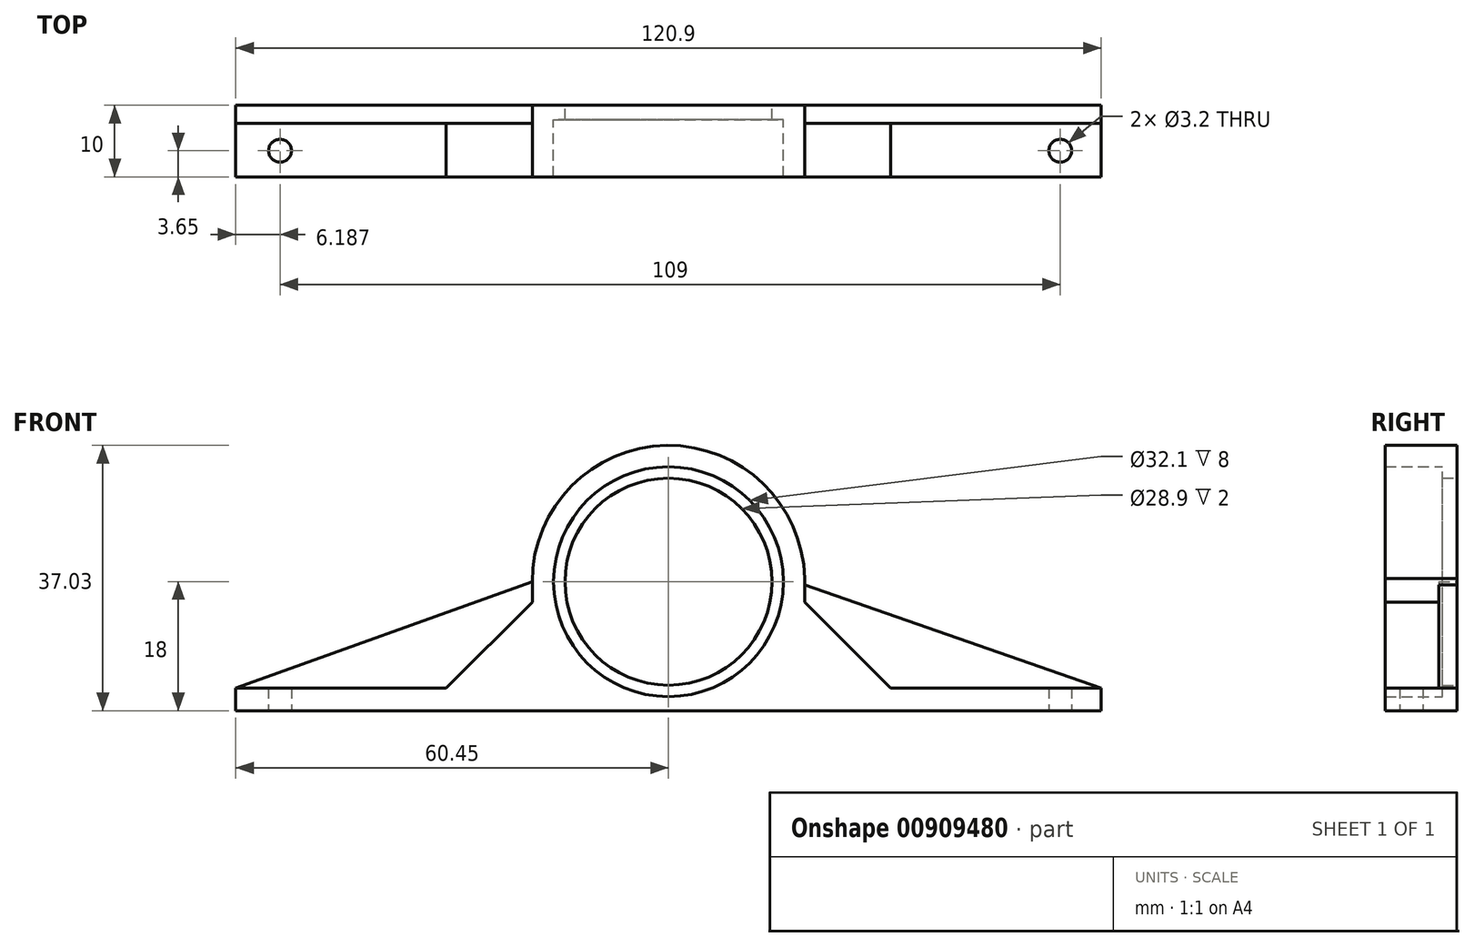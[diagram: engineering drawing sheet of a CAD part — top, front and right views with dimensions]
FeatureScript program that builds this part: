
annotation { "Feature Type Name" : "Feature", "Feature Type Description" : "" }
export const myFeature = defineFeature(function(context is Context, id is Id, definition is map)
    precondition{}
    {
        {
            var Q0;
            Q0=qCreatedBy(makeId("Front.planeOp"),FACE);
            var sketch = newSketch(context, id + "F0", { "sketchPlane" : qUnion([Q0])});
            skLineSegment(sketch, "E0.bottom", {"start": v(-60.45, 0) * mm, "end": v(-15.87, 0) * mm});
            skLineSegment(sketch, "E0.top", {"start": v(-60.45, 3.18) * mm, "end": v(-19.03, 3.18) * mm});
            skLineSegment(sketch, "E0.left", {"start": v(-60.45, 0) * mm, "end": v(-60.45, 3.18) * mm});
            skLineSegment(sketch, "E0.right", {"start": v(60.45, 0) * mm, "end": v(60.45, 3.18) * mm});
            skLineSegment(sketch, "E1.trimOffspring", {"start": v(19.02, 3.18) * mm, "end": v(60.45, 3.18) * mm});
            skLineSegment(sketch, "E2.trimOffspring", {"start": v(15.85, 0) * mm, "end": v(60.45, 0) * mm});
            skArc(sketch, "E3", {"start": v(15.85, 20.53) * mm, "mid": v(-1.27, 34) * mm, "end": v(-16.05, 18) * mm});
            skArc(sketch, "E4", {"start": v(19.02, 18.46) * mm, "mid": v(-0.23, 37.03) * mm, "end": v(-19.03, 18) * mm});
            skLineSegment(sketch, "E5", {"start": v(-19.03, 18) * mm, "end": v(-19.03, 3.18) * mm});
            skLineSegment(sketch, "E6", {"start": v(15.85, 20.53) * mm, "end": v(15.85, 20.53) * mm});
            skLineSegment(sketch, "E7", {"start": v(19.02, 18.46) * mm, "end": v(19.02, 3.18) * mm});
            skPoint(sketch, "E8.orphan", {"position": v(-19.03, 0) * mm});
            skPoint(sketch, "E9.orphan", {"position": v(19.02, 0) * mm});
            skLineSegment(sketch, "E10", {"start": v(0, 18) * mm, "end": v(0, 18) * mm});
            skCircle(sketch, "E11", {"center": v(0, 18) * mm, "radius": 16.05 * mm});
            skArc(sketch, "E12", {"start": v(19.02, 17.54) * mm, "mid": v(0.23, 37.03) * mm, "end": v(-19.03, 18) * mm});
            skLineSegment(sketch, "E13", {"start": v(-15.87, 0) * mm, "end": v(15.85, 0) * mm});
            skCircle(sketch, "E14", {"center": v(0, 18) * mm, "radius": 14.45 * mm});
            skLineSegment(sketch, "E15", {"start": v(-19.03, 18) * mm, "end": v(-60.45, 3.18) * mm});
            skLineSegment(sketch, "E16", {"start": v(19.02, 17.54) * mm, "end": v(60.45, 3.18) * mm});
            skLineSegment(sketch, "E17", {"start": v(19.02, 15.18) * mm, "end": v(31.03, 3.18) * mm});
            skLineSegment(sketch, "E18", {"start": v(-19.03, 15.18) * mm, "end": v(-31.03, 3.18) * mm});
            skSolve(sketch);
        }
        {
            var Q0;
            Q0=makeQuery(id+"F0.imprint","IMPRINT",FACE,{"disambiguationData":[TD([[makeQuery(id+"F0.imprint","IMPRINT",EDGE,{"derivedFrom":sQuery(id+"F0.wireOp",EDGE,"E0.top")}),-1.0]])]});
            extrude(context, id + "F1", {"entities" : qUnion([Q0]), "depth" : 10 * mm, "offsetDistance" : 25.4 * mm});
        }
        {
            var Q0;
            Q0=makeQuery(id+"F0.imprint","IMPRINT",FACE,{"disambiguationData":[TD([[makeQuery(id+"F0.imprint","IMPRINT",EDGE,{"derivedFrom":sQuery(id+"F0.wireOp",EDGE,"E3")}),1.0]])]});
            extrude(context, id + "F2", {"entities" : qUnion([Q0]), "operationType" : NewBodyOperationType.ADD, "depth" : 1.59 * mm, "offsetDistance" : 25.4 * mm});
        }
        {
            var Q0;
            Q0=makeQuery(id+"F1.opExtrude","SWEPT_FACE",FACE,{"disambiguationData":[OSD([sQuery(id+"F0.wireOp",EDGE,"E0.bottom")])]});
            var sketch = newSketch(context, id + "F3", { "sketchPlane" : qUnion([Q0])});
            skCircle(sketch, "E19", {"center": v(54.74, 6.35) * mm, "radius": 1.6 * mm});
            skCircle(sketch, "E20", {"center": v(-54.26, 6.35) * mm, "radius": 1.6 * mm});
            skSolve(sketch);
        }
        {
            var Q0;
            Q0=makeQuery(id+"F3.imprint","IMPRINT",FACE,{"disambiguationData":[TD([[makeQuery(id+"F3.imprint","IMPRINT",EDGE,{"derivedFrom":sQuery(id+"F3.wireOp",EDGE,"E20")}),1.0]])]});
            var Q1;
            Q1=makeQuery(id+"F3.imprint","IMPRINT",FACE,{"disambiguationData":[TD([[makeQuery(id+"F3.imprint","IMPRINT",EDGE,{"derivedFrom":sQuery(id+"F3.wireOp",EDGE,"E19")}),1.0]])]});
            var Q2;
            Q2=sQuery(id+"F3.wireOp",EDGE,"E20");
            var Q3;
            Q3=sQuery(id+"F3.wireOp",EDGE,"E19");
            extrude(context, id + "F4", {"entities" : qUnion([Q0, Q1]), "operationType" : NewBodyOperationType.REMOVE, "surfaceEntities" : qUnion([Q2, Q3]), "oppositeDirection" : true, "depth" : 6.35 * mm, "offsetDistance" : 25.4 * mm});
        }
        {
            var Q0;
            Q0=makeQuery(id+"F0.imprint","IMPRINT",FACE,{"disambiguationData":[TD([[makeQuery(id+"F0.imprint","IMPRINT",EDGE,{"derivedFrom":sQuery(id+"F0.wireOp",EDGE,"E14")}),-1.0]])]});
            extrude(context, id + "F5", {"entities" : qUnion([Q0]), "operationType" : NewBodyOperationType.ADD, "depth" : 2 * mm, "offsetDistance" : 25 * mm});
        }
        {
            var Q0;
            {var subQ0=sQuery(id+"F0.wireOp",EDGE,"E1.trimOffspring");Q0=makeQuery(id+"F0.imprint","IMPRINT",FACE,{"disambiguationData":[TD([[makeQuery(id+"F0.imprint","IMPRINT",EDGE,{"derivedFrom":subQ0}),1.0]])]});}
            var Q1;
            Q1=makeQuery(id+"F0.imprint","IMPRINT",FACE,{"disambiguationData":[TD([[makeQuery(id+"F0.imprint","IMPRINT",EDGE,{"derivedFrom":sQuery(id+"F0.wireOp",EDGE,"E0.top")}),1.0]])]});
            extrude(context, id + "F6", {"entities" : qUnion([Q0, Q1]), "operationType" : NewBodyOperationType.ADD, "depth" : 2 * mm, "offsetDistance" : 25 * mm});
        }
        {
            var Q0;
            {var subQ3=sQuery(id+"F0.wireOp",EDGE,"E17");Q0=makeQuery(id+"F0.imprint","IMPRINT",FACE,{"disambiguationData":[TD([[makeQuery(id+"F0.imprint","IMPRINT",EDGE,{"derivedFrom":subQ3}),-1.0]])]});}
            var Q1;
            {var subQ3=sQuery(id+"F0.wireOp",EDGE,"E18");Q1=makeQuery(id+"F0.imprint","IMPRINT",FACE,{"disambiguationData":[TD([[makeQuery(id+"F0.imprint","IMPRINT",EDGE,{"derivedFrom":subQ3}),1.0]])]});}
            extrude(context, id + "F7", {"entities" : qUnion([Q0, Q1]), "operationType" : NewBodyOperationType.ADD, "depth" : 10 * mm, "offsetDistance" : 25 * mm});
        }
        {
            var Q0;
            {var subQ0=sQuery(id+"F0.wireOp",EDGE,"E16");Q0=makeQuery(id+"F0.imprint","IMPRINT",FACE,{"disambiguationData":[TD([[makeQuery(id+"F0.imprint","IMPRINT",EDGE,{"derivedFrom":subQ0}),-1.0]])]});}
            var Q1;
            {var subQ0=sQuery(id+"F0.wireOp",EDGE,"E15");Q1=makeQuery(id+"F0.imprint","IMPRINT",FACE,{"disambiguationData":[TD([[makeQuery(id+"F0.imprint","IMPRINT",EDGE,{"derivedFrom":subQ0}),1.0]])]});}
            extrude(context, id + "F8", {"entities" : qUnion([Q0, Q1]), "operationType" : NewBodyOperationType.ADD, "depth" : 2.5 * mm, "offsetDistance" : 25 * mm});
        }
    });
